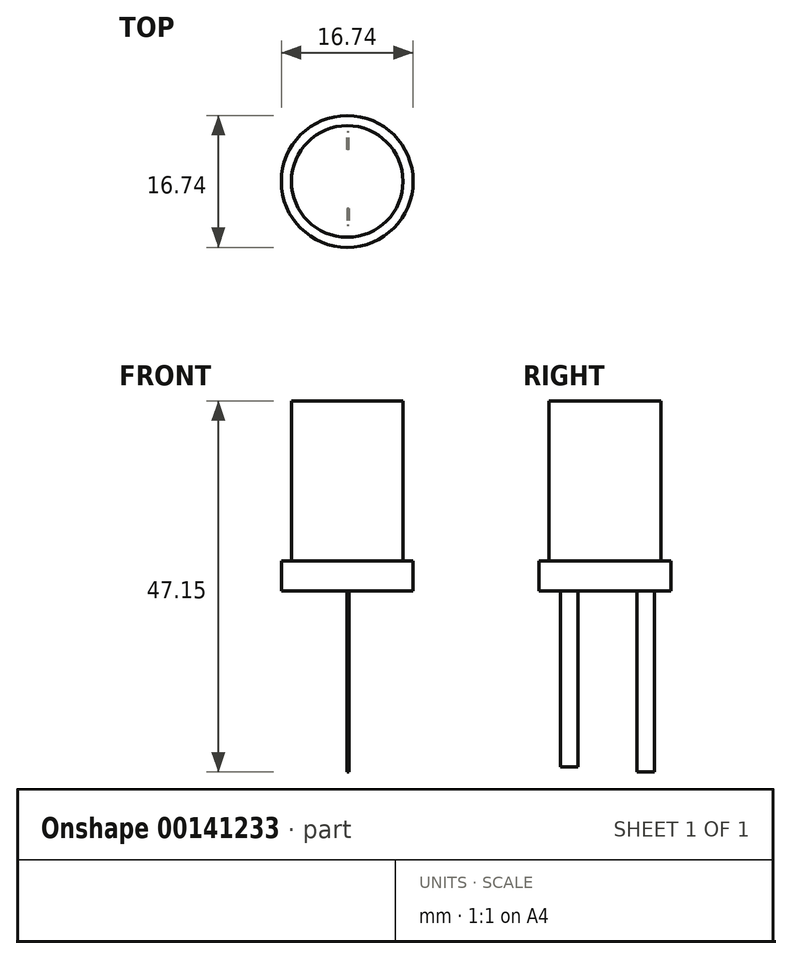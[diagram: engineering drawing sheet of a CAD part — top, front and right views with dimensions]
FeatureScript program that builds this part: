
annotation { "Feature Type Name" : "Feature", "Feature Type Description" : "" }
export const myFeature = defineFeature(function(context is Context, id is Id, definition is map)
    precondition{}
    {
        {
            var Q0;
            Q0=qCreatedBy(makeId("Top.planeOp"),FACE);
            var sketch = newSketch(context, id + "F0", { "sketchPlane" : qUnion([Q0])});
            skCircle(sketch, "E0", {"center": v(0, 0) * mm, "radius": 8.37 * mm});
            skSolve(sketch);
        }
        {
            var Q0;
            Q0 = qSketchRegion(id + "F0", true);
            extrude(context, id + "F1", {"entities" : qUnion([Q0]), "depth" : 3.8 * mm});
        }
        {
            var Q0;
            Q0=makeQuery(id+"F1.opExtrude","CAP_FACE",FACE,{"disambiguationData":[OSD([sQuery(id+"F0.wireOp",EDGE,"E0")])],"isStart":false});
            var sketch = newSketch(context, id + "F2", { "sketchPlane" : qUnion([Q0])});
            skCircle(sketch, "E1", {"center": v(0, 0) * mm, "radius": 7.08 * mm});
            skSolve(sketch);
        }
        {
            var Q0;
            Q0 = qSketchRegion(id + "F2", true);
            extrude(context, id + "F3", {"entities" : qUnion([Q0]), "operationType" : NewBodyOperationType.ADD, "depth" : 20.32 * mm});
        }
        {
            var Q0;
            Q0=qCreatedBy(makeId("Right.planeOp"),FACE);
            var sketch = newSketch(context, id + "F4", { "sketchPlane" : qUnion([Q0])});
            skLineSegment(sketch, "E2", {"start": v(6.26, 0) * mm, "end": v(6.26, -23.02) * mm});
            skLineSegment(sketch, "E3", {"start": v(6.26, -23.02) * mm, "end": v(4.07, -23.02) * mm});
            skLineSegment(sketch, "E4", {"start": v(4.07, -23.02) * mm, "end": v(4.07, 0) * mm});
            skLineSegment(sketch, "E5", {"start": v(4.07, 0) * mm, "end": v(6.26, 0) * mm});
            skSolve(sketch);
        }
        {
            var Q0;
            Q0 = qSketchRegion(id + "F4", true);
            extrude(context, id + "F5", {"entities" : qUnion([Q0]), "operationType" : NewBodyOperationType.ADD, "depth" : 0.25 * mm});
        }
        {
            var Q0;
            Q0=qCreatedBy(makeId("Right.planeOp"),FACE);
            var sketch = newSketch(context, id + "F6", { "sketchPlane" : qUnion([Q0])});
            skLineSegment(sketch, "E6", {"start": v(-5.64, 0) * mm, "end": v(-5.64, -22.4) * mm});
            skLineSegment(sketch, "E7", {"start": v(-5.64, -22.4) * mm, "end": v(-3.44, -22.4) * mm});
            skLineSegment(sketch, "E8", {"start": v(-3.44, -22.4) * mm, "end": v(-3.44, 0) * mm});
            skLineSegment(sketch, "E9", {"start": v(-3.44, 0) * mm, "end": v(-5.64, 0) * mm});
            skSolve(sketch);
        }
        {
            var Q0;
            Q0 = qSketchRegion(id + "F6", true);
            extrude(context, id + "F7", {"entities" : qUnion([Q0]), "operationType" : NewBodyOperationType.ADD, "depth" : 0.25 * mm});
        }
    });
